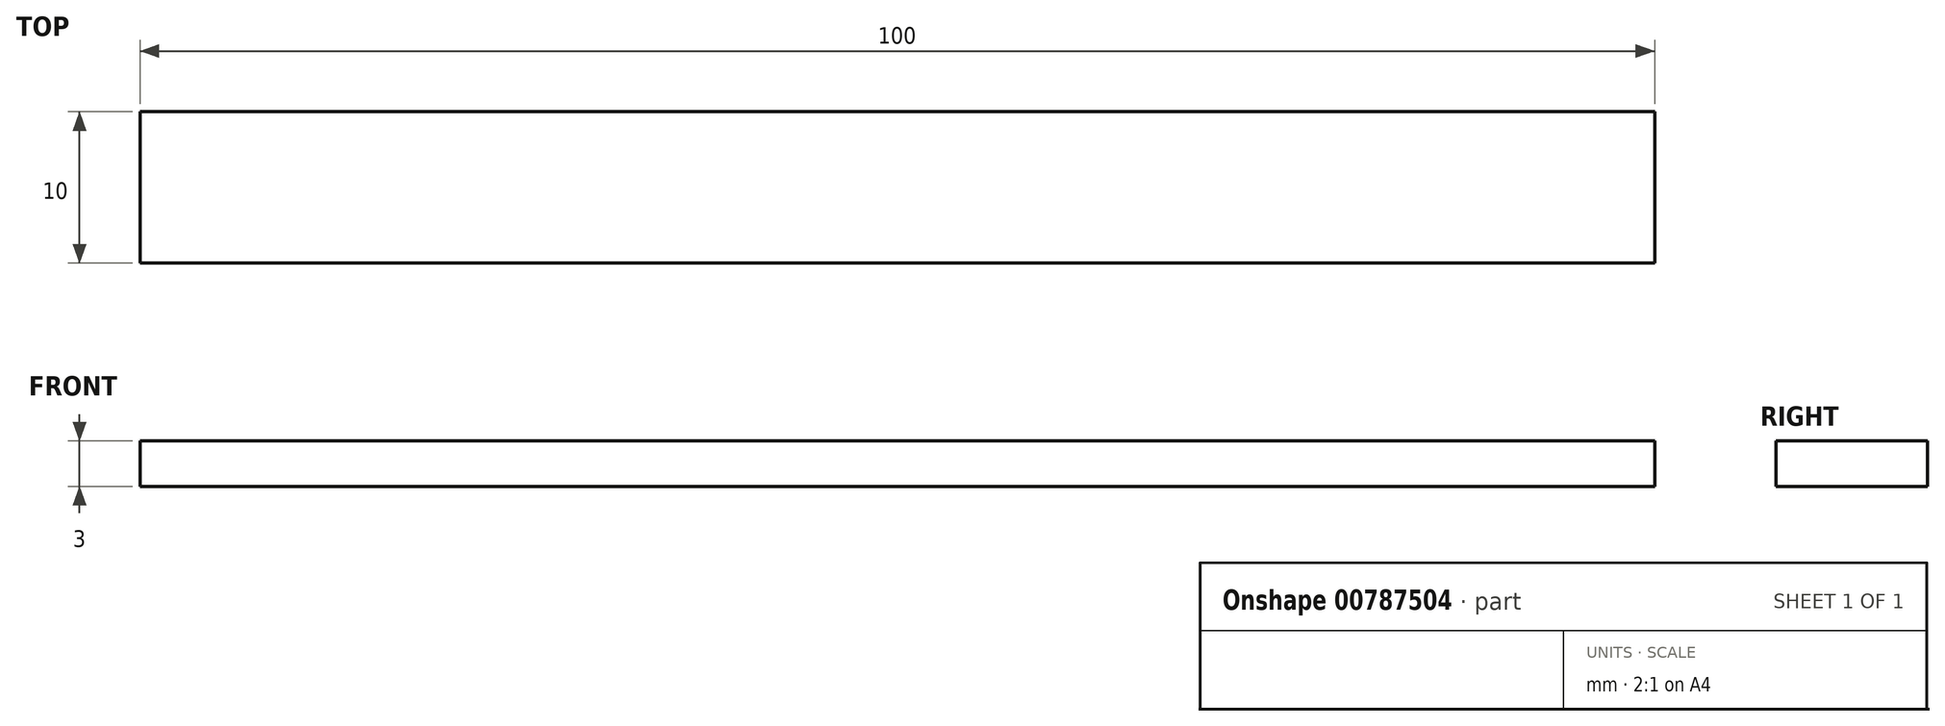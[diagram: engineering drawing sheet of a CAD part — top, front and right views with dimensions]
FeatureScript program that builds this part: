
annotation { "Feature Type Name" : "Feature", "Feature Type Description" : "" }
export const myFeature = defineFeature(function(context is Context, id is Id, definition is map)
    precondition{}
    {
        {
            var Q0;
            Q0=qCreatedBy(makeId("Top.planeOp"),FACE);
            var sketch = newSketch(context, id + "F0", { "sketchPlane" : qUnion([Q0])});
            skLineSegment(sketch, "E0.bottom", {"start": v(-34.6, -8.85) * mm, "end": v(65.4, -8.85) * mm});
            skLineSegment(sketch, "E0.top", {"start": v(-34.6, 1.15) * mm, "end": v(65.4, 1.15) * mm});
            skLineSegment(sketch, "E0.left", {"start": v(-34.6, -8.85) * mm, "end": v(-34.6, 1.15) * mm});
            skLineSegment(sketch, "E0.right", {"start": v(65.4, -8.85) * mm, "end": v(65.4, 1.15) * mm});
            skSolve(sketch);
        }
        {
            var Q0;
            Q0=makeQuery(id+"F0.imprint","IMPRINT",FACE,{"disambiguationData":[TD([[makeQuery(id+"F0.imprint","IMPRINT",EDGE,{"derivedFrom":sQuery(id+"F0.wireOp",EDGE,"E0.bottom")}),1.0]])]});
            extrude(context, id + "F1", {"entities" : qUnion([Q0]), "depth" : 3 * mm, "offsetDistance" : 25.4 * mm});
        }
    });
